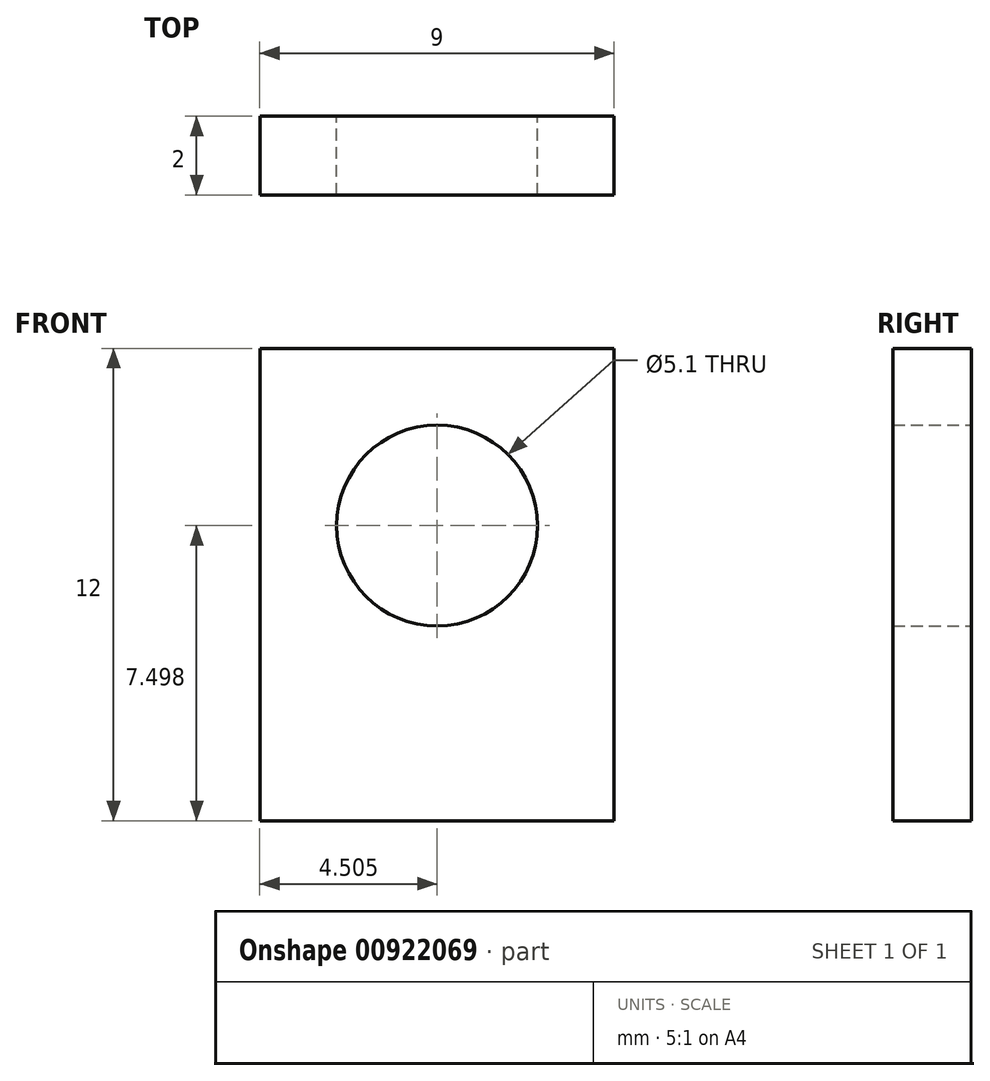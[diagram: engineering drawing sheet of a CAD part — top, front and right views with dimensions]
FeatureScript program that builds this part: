
annotation { "Feature Type Name" : "Feature", "Feature Type Description" : "" }
export const myFeature = defineFeature(function(context is Context, id is Id, definition is map)
    precondition{}
    {
        {
            var Q0;
            Q0=qCreatedBy(makeId("Front.planeOp"),FACE);
            var sketch = newSketch(context, id + "F0", { "sketchPlane" : qUnion([Q0])});
            skLineSegment(sketch, "E0.bottom", {"start": v(-21.65, 10.3) * mm, "end": v(-12.65, 10.3) * mm});
            skLineSegment(sketch, "E0.top", {"start": v(-21.65, -1.7) * mm, "end": v(-12.65, -1.7) * mm});
            skLineSegment(sketch, "E0.left", {"start": v(-21.65, 10.3) * mm, "end": v(-21.65, -1.7) * mm});
            skLineSegment(sketch, "E0.right", {"start": v(-12.65, 10.3) * mm, "end": v(-12.65, -1.7) * mm});
            skCircle(sketch, "E1", {"center": v(-17.15, 5.8) * mm, "radius": 2.55 * mm});
            skSolve(sketch);
        }
        {
            var Q0;
            Q0 = qSketchRegion(id + "F0", true);
            extrude(context, id + "F1", {"entities" : qUnion([Q0]), "depth" : 2 * mm, "offsetDistance" : 25 * mm});
        }
    });
